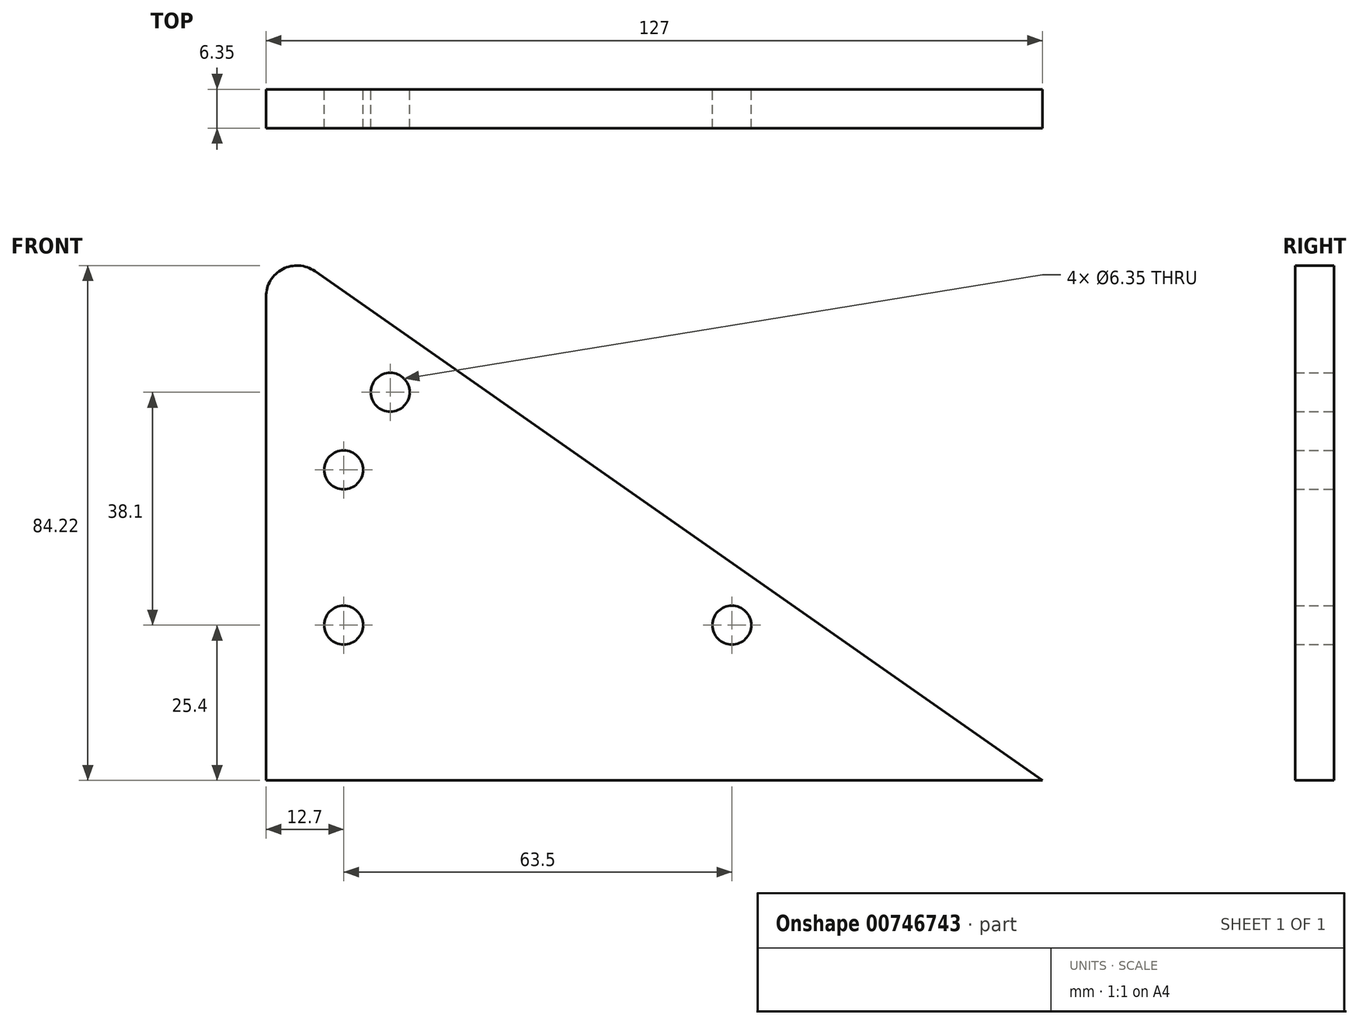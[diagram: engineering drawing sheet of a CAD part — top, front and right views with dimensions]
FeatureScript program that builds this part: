
annotation { "Feature Type Name" : "Feature", "Feature Type Description" : "" }
export const myFeature = defineFeature(function(context is Context, id is Id, definition is map)
    precondition{}
    {
        {
            var Q0;
            Q0=qCreatedBy(makeId("Front.planeOp"),FACE);
            var sketch = newSketch(context, id + "F0", { "sketchPlane" : qUnion([Q0])});
            skLineSegment(sketch, "E0", {"start": v(0, 79.14) * mm, "end": v(0, 0) * mm});
            skLineSegment(sketch, "E1", {"start": v(0, 0) * mm, "end": v(127, 0) * mm});
            skLineSegment(sketch, "E2", {"start": v(127, 0) * mm, "end": v(8, 83.3) * mm});
            skCircle(sketch, "E3", {"center": v(12.7, 25.4) * mm, "radius": 3.18 * mm});
            skCircle(sketch, "E4", {"center": v(12.7, 50.8) * mm, "radius": 3.18 * mm});
            skCircle(sketch, "E5", {"center": v(76.2, 25.4) * mm, "radius": 3.18 * mm});
            skCircle(sketch, "E6", {"center": v(20.32, 63.5) * mm, "radius": 3.18 * mm});
            skPoint(sketch, "E7.visualSharp", {"position": v(0, 88.9) * mm});
            skArc(sketch, "E7.filletArc", {"start": v(8, 83.3) * mm, "mid": v(2.73, 83.65) * mm, "end": v(0, 79.14) * mm});
            skSolve(sketch);
        }
        {
            var Q0;
            Q0=makeQuery(id+"F0.imprint","IMPRINT",FACE,{"disambiguationData":[TD([[makeQuery(id+"F0.imprint","IMPRINT",EDGE,{"derivedFrom":sQuery(id+"F0.wireOp",EDGE,"E0")}),1.0]])]});
            extrude(context, id + "F1", {"entities" : qUnion([Q0]), "depth" : 6.35 * mm, "offsetDistance" : 25.4 * mm});
        }
    });
